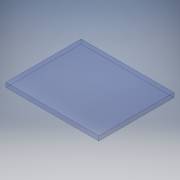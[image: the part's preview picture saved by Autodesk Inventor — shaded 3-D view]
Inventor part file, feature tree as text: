
AUTODESK INVENTOR PART (.ipt)
format: ipt  version: 2019.3 (Build 233278000, 278)  size: 95,744 bytes
history: native  units: mm
features: other x1, extrude x1, sketch x1
ambient origin geometry x8: Origin, YZ Plane, XZ Plane, XY Plane, X Axis, Y Axis, Z Axis, Center Point
bodies: Body1 (feature_tree)
feature tree (3):
  other  "ソリッド1"
  extrude  "押し出し1"  Depth=2100.0mm
  sketch  "スケッチ1"
